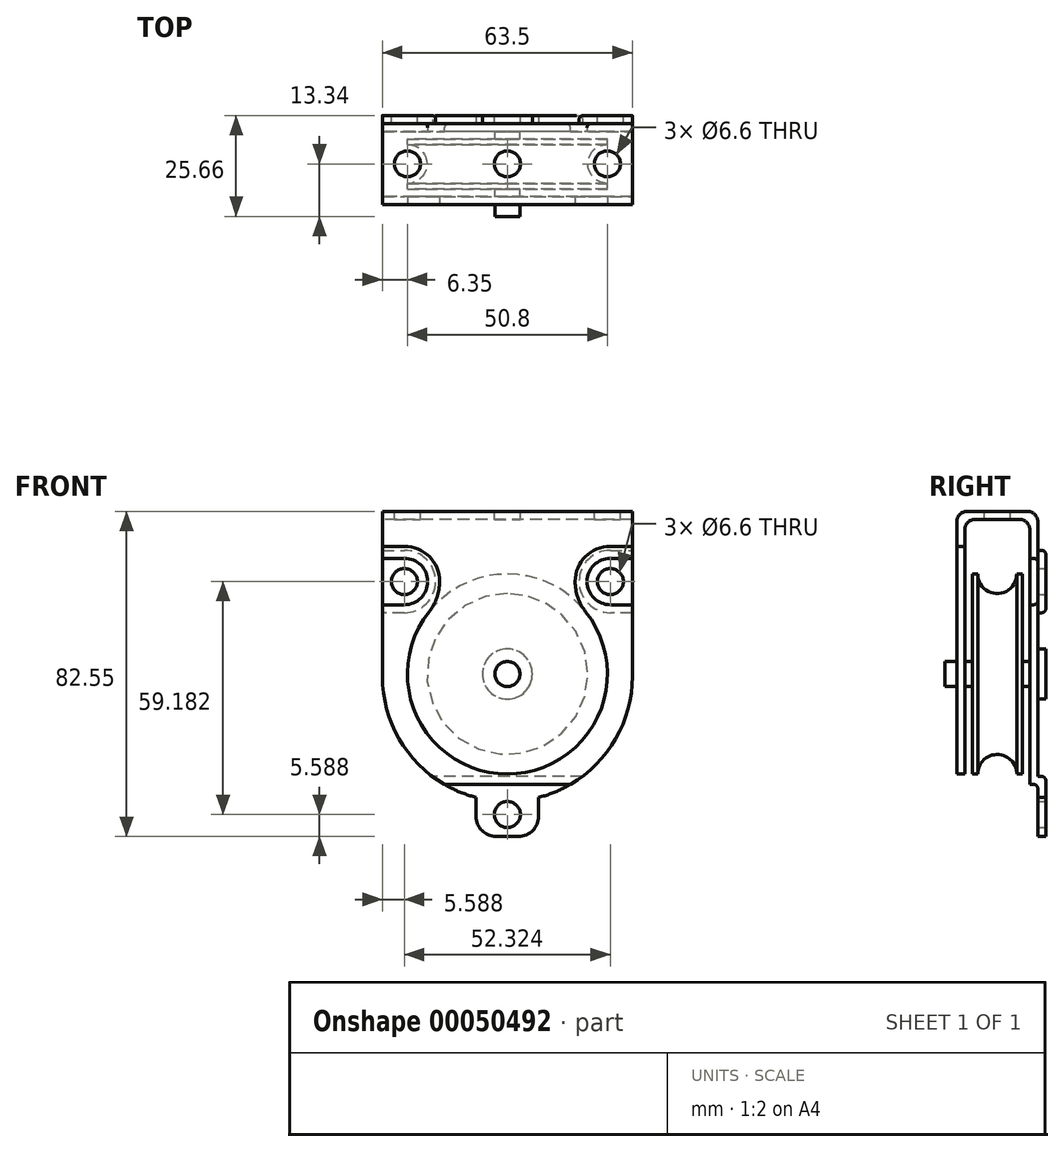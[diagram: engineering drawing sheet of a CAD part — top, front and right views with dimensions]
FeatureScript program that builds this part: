
annotation { "Feature Type Name" : "Feature", "Feature Type Description" : "" }
export const myFeature = defineFeature(function(context is Context, id is Id, definition is map)
    precondition{}
    {
        {
            var Q0;
            Q0=qCreatedBy(makeId("Front.planeOp"),FACE);
            var sketch = newSketch(context, id + "F0", { "sketchPlane" : qUnion([Q0])});
            skLineSegment(sketch, "E0.rect.bottom", {"start": v(31.75, 36.83) * mm, "end": v(-31.75, 36.83) * mm});
            skLineSegment(sketch, "E0.rect.left", {"start": v(31.75, 36.83) * mm, "end": v(31.75, -5.08) * mm});
            skLineSegment(sketch, "E0.rect.right", {"start": v(-31.75, 36.83) * mm, "end": v(-31.75, -5.08) * mm});
            skPoint(sketch, "E0.rect.middle", {"position": v(0, 0) * mm});
            skArc(sketch, "E1", {"start": v(-31.75, -5.08) * mm, "mid": v(0, -36.83) * mm, "end": v(31.75, -5.08) * mm});
            skPoint(sketch, "E2.orphan", {"position": v(-31.75, -36.83) * mm});
            skPoint(sketch, "E3.orphan", {"position": v(31.75, -36.83) * mm});
            skLineSegment(sketch, "E4", {"start": v(31.75, -5.08) * mm, "end": v(31.75, -36.83) * mm, "construction": true});
            skLineSegment(sketch, "E5", {"start": v(31.75, -36.83) * mm, "end": v(0, -36.83) * mm, "construction": true});
            skLineSegment(sketch, "E6", {"start": v(0, -36.83) * mm, "end": v(-31.75, -36.83) * mm, "construction": true});
            skLineSegment(sketch, "E7", {"start": v(-31.75, -36.83) * mm, "end": v(-31.75, -5.08) * mm, "construction": true});
            skSolve(sketch);
        }
        {
            var Q0;
            Q0 = qSketchRegion(id + "F0", true);
            extrude(context, id + "F1", {"entities" : qUnion([Q0]), "endBound" : BoundingType.SYMMETRIC, "depth" : 20.57 * mm});
        }
        {
            var Q0;
            Q0=makeQuery(id+"F1.opExtrude","CAP_FACE",FACE,{"disambiguationData":[OSD([sQuery(id+"F0.wireOp",EDGE,"E0.rect.bottom"),sQuery(id+"F0.wireOp",EDGE,"E0.rect.left"),sQuery(id+"F0.wireOp",EDGE,"E0.rect.right"),sQuery(id+"F0.wireOp",EDGE,"E1")])],"isStart":true});
            var sketch = newSketch(context, id + "F2", { "sketchPlane" : qUnion([Q0])});
            skArc(sketch, "E8", {"start": v(-19.05, -30.48) * mm, "mid": v(-13.76, -33.7) * mm, "end": v(-7.94, -35.82) * mm});
            skLineSegment(sketch, "E9", {"start": v(-19.05, -30.48) * mm, "end": v(19.05, -30.48) * mm});
            skLineSegment(sketch, "E10", {"start": v(-7.94, -35.82) * mm, "end": v(-7.94, -40.64) * mm});
            skLineSegment(sketch, "E11", {"start": v(-2.86, -45.72) * mm, "end": v(2.86, -45.72) * mm});
            skLineSegment(sketch, "E12", {"start": v(7.94, -40.64) * mm, "end": v(7.94, -35.82) * mm});
            skLineSegment(sketch, "E13", {"start": v(0, -5.08) * mm, "end": v(0, -45.72) * mm, "construction": true});
            skArc(sketch, "E14.trimOffspring", {"start": v(7.94, -35.82) * mm, "mid": v(13.76, -33.7) * mm, "end": v(19.05, -30.48) * mm});
            skPoint(sketch, "E15.visualSharp", {"position": v(-7.94, -45.72) * mm});
            skArc(sketch, "E15.filletArc", {"start": v(-7.94, -40.64) * mm, "mid": v(-6.45, -44.23) * mm, "end": v(-2.86, -45.72) * mm});
            skPoint(sketch, "E16.visualSharp", {"position": v(7.94, -45.72) * mm});
            skArc(sketch, "E16.filletArc", {"start": v(2.86, -45.72) * mm, "mid": v(6.45, -44.23) * mm, "end": v(7.94, -40.64) * mm});
            skLineSegment(sketch, "E17", {"start": v(-31.75, 26.99) * mm, "end": v(-31.75, 11.11) * mm});
            skLineSegment(sketch, "E18", {"start": v(-31.75, 11.11) * mm, "end": v(-26.16, 11.11) * mm});
            skLineSegment(sketch, "E19", {"start": v(31.75, 11.11) * mm, "end": v(31.75, 26.99) * mm});
            skLineSegment(sketch, "E20", {"start": v(31.75, 26.99) * mm, "end": v(26.16, 26.99) * mm});
            skArc(sketch, "E21", {"start": v(-26.16, 11.11) * mm, "mid": v(-18.22, 19.05) * mm, "end": v(-26.16, 26.99) * mm});
            skArc(sketch, "E22", {"start": v(26.16, 26.99) * mm, "mid": v(18.22, 19.05) * mm, "end": v(26.16, 11.11) * mm});
            skLineSegment(sketch, "E23.trimOffspring", {"start": v(-26.16, 26.99) * mm, "end": v(-31.75, 26.99) * mm});
            skLineSegment(sketch, "E24.trimOffspring", {"start": v(26.16, 11.11) * mm, "end": v(31.75, 11.11) * mm});
            skSolve(sketch);
        }
        {
            var Q0;
            Q0 = qSketchRegion(id + "F2", true);
            extrude(context, id + "F3", {"entities" : qUnion([Q0]), "operationType" : NewBodyOperationType.ADD, "depth" : 2.03 * mm});
        }
        {
            var Q0;
            Q0=makeQuery(id+"F3.boolean.opBoolean","MERGE",FACE,{"derivedFrom":[makeQuery(id+"F1.opExtrude","SWEPT_FACE",FACE,{"disambiguationData":[OSD([sQuery(id+"F0.wireOp",EDGE,"E0.rect.left")])]}),makeQuery(id+"F3.opExtrude","SWEPT_FACE",FACE,{"disambiguationData":[OSD([sQuery(id+"F2.wireOp",EDGE,"E17")])]})]});
            var Q1;
            Q1=makeQuery(id+"F3.boolean.opBoolean","MERGE",FACE,{"derivedFrom":[makeQuery(id+"F1.opExtrude","SWEPT_FACE",FACE,{"disambiguationData":[OSD([sQuery(id+"F0.wireOp",EDGE,"E1")])]}),makeQuery(id+"F3.opExtrude","SWEPT_FACE",FACE,{"disambiguationData":[OSD([sQuery(id+"F2.wireOp",EDGE,"E8")])]}),makeQuery(id+"F3.opExtrude","SWEPT_FACE",FACE,{"disambiguationData":[OSD([sQuery(id+"F2.wireOp",EDGE,"E14.trimOffspring")])]})]});
            var Q2;
            Q2=makeQuery(id+"F3.boolean.opBoolean","MERGE",FACE,{"derivedFrom":[makeQuery(id+"F1.opExtrude","SWEPT_FACE",FACE,{"disambiguationData":[OSD([sQuery(id+"F0.wireOp",EDGE,"E0.rect.right")])]}),makeQuery(id+"F3.opExtrude","SWEPT_FACE",FACE,{"disambiguationData":[OSD([sQuery(id+"F2.wireOp",EDGE,"E19")])]})]});
            shell(context, id + "F4", {"entities" : qUnion([Q0, Q1, Q2]), "thickness" : 2.03 * mm});
        }
        {
            var Q0;
            Q0=makeQuery(id+"F3.opExtrude","CAP_FACE",FACE,{"disambiguationData":[OSD([sQuery(id+"F2.wireOp",EDGE,"E19"),sQuery(id+"F2.wireOp",EDGE,"E20"),sQuery(id+"F2.wireOp",EDGE,"E22"),sQuery(id+"F2.wireOp",EDGE,"E24.trimOffspring")])],"isStart":false});
            var sketch = newSketch(context, id + "F5", { "sketchPlane" : qUnion([Q0])});
            skCircle(sketch, "E25", {"center": v(26.16, 19.05) * mm, "radius": 3.3 * mm});
            skCircle(sketch, "E26", {"center": v(-26.16, 19.05) * mm, "radius": 3.3 * mm});
            skCircle(sketch, "E27", {"center": v(0, -40.13) * mm, "radius": 3.3 * mm});
            skSolve(sketch);
        }
        {
            var Q0;
            Q0 = qSketchRegion(id + "F5", true);
            extrude(context, id + "F6", {"entities" : qUnion([Q0]), "operationType" : NewBodyOperationType.REMOVE, "endBound" : BoundingType.UP_TO_NEXT, "oppositeDirection" : true, "depth" : 25.4 * mm});
        }
        {
            var Q0;
            Q0=makeQuery(id+"F1.opExtrude","CAP_FACE",FACE,{"disambiguationData":[OSD([sQuery(id+"F0.wireOp",EDGE,"E0.rect.bottom"),sQuery(id+"F0.wireOp",EDGE,"E0.rect.left"),sQuery(id+"F0.wireOp",EDGE,"E0.rect.right"),sQuery(id+"F0.wireOp",EDGE,"E1")])],"isStart":true});
            var sketch = newSketch(context, id + "F7", { "sketchPlane" : qUnion([Q0])});
            skCircle(sketch, "E28", {"center": v(0, -4.45) * mm, "radius": 6.35 * mm});
            skSolve(sketch);
        }
        {
            var Q0;
            Q0 = qSketchRegion(id + "F7", true);
            extrude(context, id + "F8", {"entities" : qUnion([Q0]), "operationType" : NewBodyOperationType.ADD, "depth" : 2.03 * mm});
        }
        {
            var Q0;
            {var subQ0=sQuery(id+"F0.wireOp",EDGE,"E1");var subQ1=sQuery(id+"F0.wireOp",EDGE,"E0.rect.right");var subQ2=sQuery(id+"F0.wireOp",EDGE,"E0.rect.left");var subQ3=sQuery(id+"F0.wireOp",EDGE,"E0.rect.bottom");Q0=makeQuery(id+"F4.opShell","OFFSET_FACE",FACE,{"disambiguationData":[OSD([subQ3,subQ2,subQ1,subQ0]),TDD([makeQuery(id+"F1.opExtrude","CAP_FACE",FACE,{"disambiguationData":[OSD([subQ3,subQ2,subQ1,subQ0])],"isStart":true})])]});}
            var sketch = newSketch(context, id + "F9", { "sketchPlane" : qUnion([Q0])});
            skCircle(sketch, "E29", {"center": v(0, -4.45) * mm, "radius": 3.18 * mm});
            skSolve(sketch);
        }
        {
            var Q0;
            Q0 = qSketchRegion(id + "F9", true);
            extrude(context, id + "F10", {"entities" : qUnion([Q0]), "operationType" : NewBodyOperationType.ADD, "depth" : 21.59 * mm});
        }
        {
            var Q0;
            Q0=qCreatedBy(makeId("Right.planeOp"),FACE);
            var sketch = newSketch(context, id + "F11", { "sketchPlane" : qUnion([Q0])});
            skLineSegment(sketch, "E30", {"start": v(-6.35, -4.45) * mm, "end": v(-6.35, 20.96) * mm});
            skLineSegment(sketch, "E31", {"start": v(-6.35, 20.96) * mm, "end": v(-4.95, 20.96) * mm});
            skLineSegment(sketch, "E32", {"start": v(4.95, 20.96) * mm, "end": v(6.35, 20.96) * mm});
            skLineSegment(sketch, "E33", {"start": v(6.35, 20.96) * mm, "end": v(6.35, -4.45) * mm});
            skArc(sketch, "E34", {"start": v(-4.95, 20.95) * mm, "mid": v(0, 16) * mm, "end": v(4.95, 20.95) * mm});
            skLineSegment(sketch, "E35", {"start": v(-6.35, -4.45) * mm, "end": v(6.35, -4.45) * mm});
            skLineSegment(sketch, "E36.0", {"start": v(-13.34, -7.62) * mm, "end": v(-13.34, -1.27) * mm, "construction": true});
            skLineSegment(sketch, "E37", {"start": v(-13.34, -4.45) * mm, "end": v(-32.86, -4.45) * mm, "construction": true});
            skPoint(sketch, "E37.endSnap0", {"position": v(-13.34, -4.45) * mm});
            skLineSegment(sketch, "E38", {"start": v(-13.34, -4.45) * mm, "end": v(-6.35, -4.45) * mm, "construction": true});
            skSolve(sketch);
        }
        {
            var Q0;
            Q0 = qSketchRegion(id + "F11", true);
            var Q1;
            Q1=sQuery(id+"F11.wireOp",EDGE,"E37");
            revolve(context, id + "F12", {"operationType" : NewBodyOperationType.ADD, "entities" : qUnion([Q0]), "axis" : qUnion([Q1]), "revolveType" : RevolveType.FULL});
        }
        {
            var Q0;
            Q0=makeQuery(id+"F1.opExtrude","SWEPT_FACE",FACE,{"disambiguationData":[OSD([sQuery(id+"F0.wireOp",EDGE,"E0.rect.bottom")])]});
            var sketch = newSketch(context, id + "F13", { "sketchPlane" : qUnion([Q0])});
            skCircle(sketch, "E39", {"center": v(-25.4, 0) * mm, "radius": 3.3 * mm});
            skCircle(sketch, "E40", {"center": v(0, 0) * mm, "radius": 3.3 * mm});
            skCircle(sketch, "E41", {"center": v(25.4, 0) * mm, "radius": 3.3 * mm});
            skLineSegment(sketch, "E42", {"start": v(-25.4, 0) * mm, "end": v(0, 0) * mm, "construction": true});
            skLineSegment(sketch, "E43", {"start": v(0, 0) * mm, "end": v(25.4, 0) * mm, "construction": true});
            skSolve(sketch);
        }
        {
            var Q0;
            Q0 = qSketchRegion(id + "F13", true);
            extrude(context, id + "F14", {"entities" : qUnion([Q0]), "operationType" : NewBodyOperationType.REMOVE, "endBound" : BoundingType.UP_TO_NEXT, "oppositeDirection" : true, "depth" : 25.4 * mm});
        }
        {
            var Q0;
            Q0=makeQuery(id+"F3.opExtrude","CAP_EDGE",EDGE,{"disambiguationData":[OSD([sQuery(id+"F2.wireOp",EDGE,"E23.trimOffspring")])],"isStart":true});
            var Q1;
            Q1=makeQuery(id+"F3.opExtrude","CAP_EDGE",EDGE,{"disambiguationData":[OSD([sQuery(id+"F2.wireOp",EDGE,"E23.trimOffspring")])],"isStart":false});
            var Q2;
            Q2=makeQuery(id+"F3.opExtrude","CAP_EDGE",EDGE,{"disambiguationData":[OSD([sQuery(id+"F2.wireOp",EDGE,"E20")])],"isStart":true});
            var Q3;
            Q3=makeQuery(id+"F3.opExtrude","CAP_EDGE",EDGE,{"disambiguationData":[OSD([sQuery(id+"F2.wireOp",EDGE,"E20")])],"isStart":false});
            var Q4;
            {var subQ0=sQuery(id+"F2.wireOp",EDGE,"E18");Q4=makeQuery(id+"F4.opShell","OFFSET_EDGE",EDGE,{"disambiguationData":[OSD([subQ0]),TDD([makeQuery(id+"F3.opExtrude","CAP_EDGE",EDGE,{"disambiguationData":[OSD([subQ0])],"isStart":false})])]});}
            var Q5;
            {var subQ0=sQuery(id+"F2.wireOp",EDGE,"E18");Q5=makeQuery(id+"F4.opShell","OFFSET_EDGE",EDGE,{"disambiguationData":[OSD([subQ0]),TDD([makeQuery(id+"F3.opExtrude","CAP_EDGE",EDGE,{"disambiguationData":[OSD([subQ0])],"isStart":true})])]});}
            var Q6;
            {var subQ0=sQuery(id+"F2.wireOp",EDGE,"E24.trimOffspring");Q6=makeQuery(id+"F4.opShell","OFFSET_EDGE",EDGE,{"disambiguationData":[OSD([subQ0]),TDD([makeQuery(id+"F3.opExtrude","CAP_EDGE",EDGE,{"disambiguationData":[OSD([subQ0])],"isStart":false})])]});}
            var Q7;
            {var subQ0=sQuery(id+"F2.wireOp",EDGE,"E24.trimOffspring");Q7=makeQuery(id+"F4.opShell","OFFSET_EDGE",EDGE,{"disambiguationData":[OSD([subQ0]),TDD([makeQuery(id+"F3.opExtrude","CAP_EDGE",EDGE,{"disambiguationData":[OSD([subQ0])],"isStart":true})])]});}
            fillet(context, id + "F15", {"entities" : qUnion([Q0, Q1, Q2, Q3, Q4, Q5, Q6, Q7]), "radius" : 1.02 * mm, "tangentPropagation" : true, "allowEdgeOverflow" : false});
        }
        {
            var Q0;
            Q0=makeQuery(id+"F3.opExtrude","CAP_EDGE",EDGE,{"disambiguationData":[OSD([sQuery(id+"F2.wireOp",EDGE,"E9")])],"isStart":true});
            var Q1;
            Q1=makeQuery(id+"F3.opExtrude","CAP_EDGE",EDGE,{"disambiguationData":[OSD([sQuery(id+"F2.wireOp",EDGE,"E9")])],"isStart":false});
            var Q2;
            {var subQ0=sQuery(id+"F2.wireOp",EDGE,"E9");Q2=makeQuery(id+"F4.opShell","OFFSET_EDGE",EDGE,{"disambiguationData":[OSD([subQ0]),TDD([makeQuery(id+"F3.opExtrude","CAP_EDGE",EDGE,{"disambiguationData":[OSD([subQ0])],"isStart":false})])]});}
            var Q3;
            {var subQ0=sQuery(id+"F2.wireOp",EDGE,"E9");Q3=makeQuery(id+"F4.opShell","OFFSET_EDGE",EDGE,{"disambiguationData":[OSD([subQ0]),TDD([makeQuery(id+"F3.opExtrude","CAP_EDGE",EDGE,{"disambiguationData":[OSD([subQ0])],"isStart":true})])]});}
            fillet(context, id + "F16", {"entities" : qUnion([Q0, Q1, Q2, Q3]), "radius" : 1.02 * mm, "tangentPropagation" : true, "allowEdgeOverflow" : false});
        }
        {
            var Q0;
            Q0=makeQuery(id+"F1.opExtrude","CAP_EDGE",EDGE,{"disambiguationData":[OSD([sQuery(id+"F0.wireOp",EDGE,"E0.rect.bottom")])],"isStart":true});
            var Q1;
            Q1=makeQuery(id+"F1.opExtrude","CAP_EDGE",EDGE,{"disambiguationData":[OSD([sQuery(id+"F0.wireOp",EDGE,"E0.rect.bottom")])],"isStart":false});
            var Q2;
            {var subQ0=sQuery(id+"F0.wireOp",EDGE,"E0.rect.bottom");Q2=makeQuery(id+"F4.opShell","OFFSET_EDGE",EDGE,{"disambiguationData":[OSD([subQ0]),TDD([makeQuery(id+"F1.opExtrude","CAP_EDGE",EDGE,{"disambiguationData":[OSD([subQ0])],"isStart":true})])]});}
            var Q3;
            {var subQ0=sQuery(id+"F0.wireOp",EDGE,"E0.rect.bottom");Q3=makeQuery(id+"F4.opShell","OFFSET_EDGE",EDGE,{"disambiguationData":[OSD([subQ0]),TDD([makeQuery(id+"F1.opExtrude","CAP_EDGE",EDGE,{"disambiguationData":[OSD([subQ0])],"isStart":false})])]});}
            fillet(context, id + "F17", {"entities" : qUnion([Q0, Q1, Q2, Q3]), "radius" : 2.54 * mm, "tangentPropagation" : true, "allowEdgeOverflow" : false});
        }
        {
            var Q0;
            Q0=makeQuery(id+"F1.opExtrude","CAP_FACE",FACE,{"disambiguationData":[OSD([sQuery(id+"F0.wireOp",EDGE,"E0.rect.bottom"),sQuery(id+"F0.wireOp",EDGE,"E0.rect.left"),sQuery(id+"F0.wireOp",EDGE,"E0.rect.right"),sQuery(id+"F0.wireOp",EDGE,"E1")])],"isStart":false});
            var sketch = newSketch(context, id + "F18", { "sketchPlane" : qUnion([Q0])});
            skArc(sketch, "E44.0.0", {"start": v(-19.9, 11.35) * mm, "mid": v(0, -29.85) * mm, "end": v(19.9, 11.35) * mm});
            skLineSegment(sketch, "E45.0", {"start": v(31.75, 28) * mm, "end": v(26.16, 28) * mm});
            skArc(sketch, "E46.0", {"start": v(26.16, 28) * mm, "mid": v(17.2, 19.05) * mm, "end": v(26.16, 10.1) * mm});
            skArc(sketch, "E47.0", {"start": v(-17.2, 19.05) * mm, "mid": v(-19.83, 25.38) * mm, "end": v(-26.16, 28) * mm});
            skLineSegment(sketch, "E48.0", {"start": v(-26.16, 28) * mm, "end": v(-31.75, 28) * mm});
            skArc(sketch, "E49", {"start": v(17.2, 19.05) * mm, "mid": v(17.9, 14.97) * mm, "end": v(19.9, 11.35) * mm});
            skArc(sketch, "E50", {"start": v(-19.9, 11.35) * mm, "mid": v(-17.9, 14.97) * mm, "end": v(-17.2, 19.05) * mm});
            skPoint(sketch, "E51.orphan", {"position": v(-26.16, 10.1) * mm});
            skLineSegment(sketch, "E52.0", {"start": v(31.75, 28) * mm, "end": v(31.75, -5.08) * mm});
            skArc(sketch, "E53.0", {"start": v(-31.75, -5.08) * mm, "mid": v(0, -36.83) * mm, "end": v(31.75, -5.08) * mm});
            skLineSegment(sketch, "E54.0", {"start": v(-31.75, 28) * mm, "end": v(-31.75, -5.08) * mm});
            skPoint(sketch, "E55.orphan", {"position": v(31.75, 34.3) * mm});
            skPoint(sketch, "E56.orphan", {"position": v(-31.75, 34.3) * mm});
            skSolve(sketch);
        }
        {
            var Q0;
            Q0 = qSketchRegion(id + "F18", true);
            extrude(context, id + "F19", {"entities" : qUnion([Q0]), "operationType" : NewBodyOperationType.REMOVE, "endBound" : BoundingType.UP_TO_NEXT, "oppositeDirection" : true, "depth" : 25.4 * mm});
        }
    });
